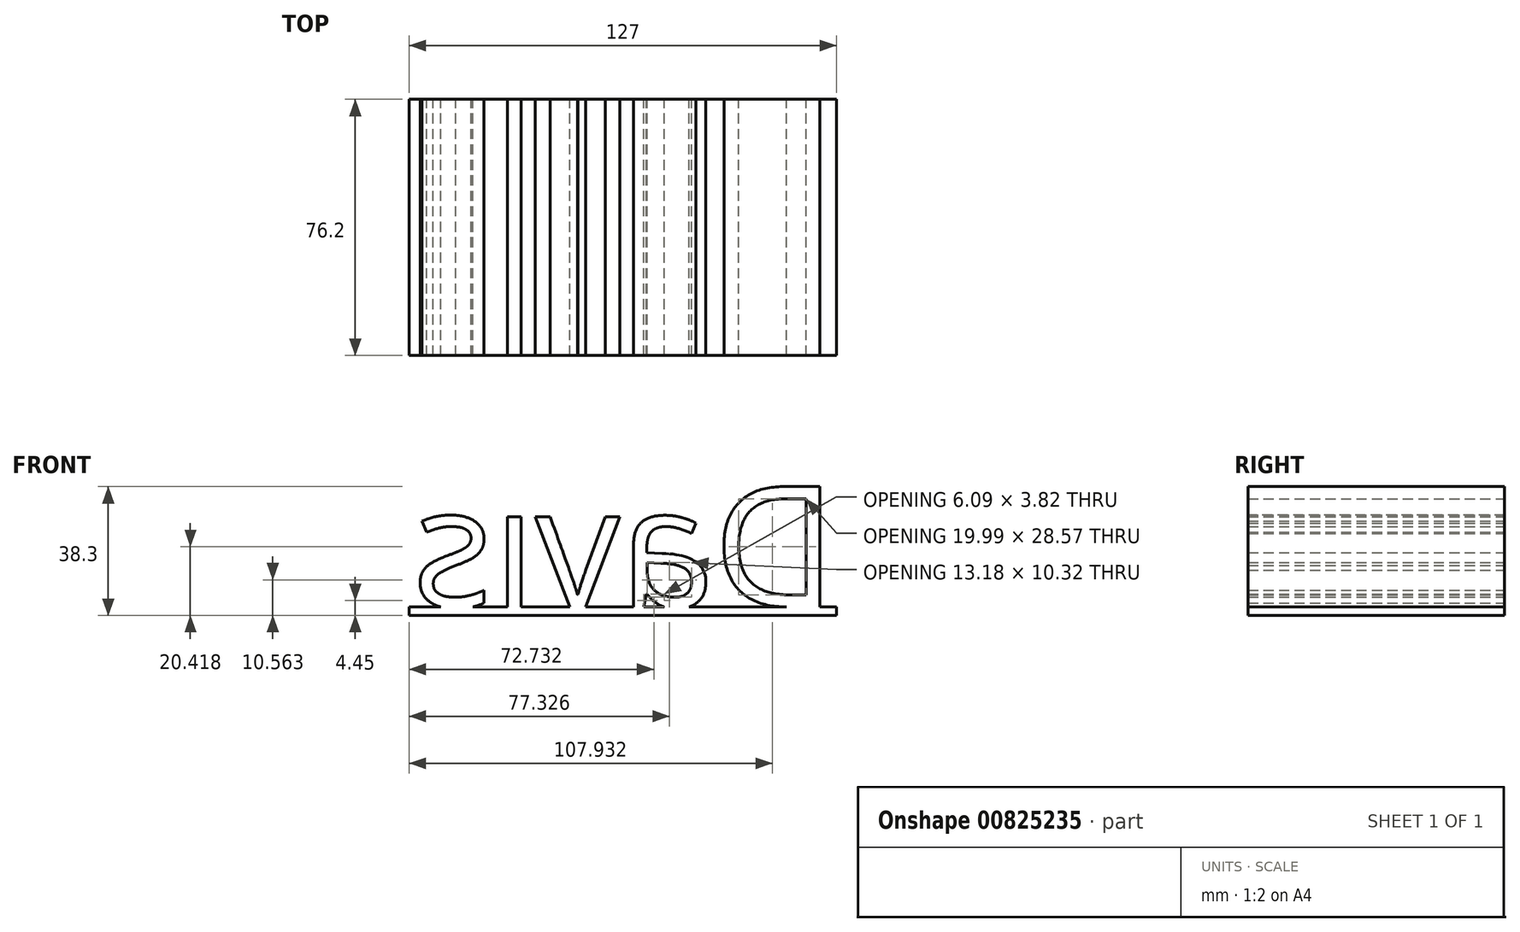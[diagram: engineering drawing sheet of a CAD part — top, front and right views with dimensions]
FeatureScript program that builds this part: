
annotation { "Feature Type Name" : "Feature", "Feature Type Description" : "" }
export const myFeature = defineFeature(function(context is Context, id is Id, definition is map)
    precondition{}
    {
        {
            var Q0;
            Q0=qCreatedBy(makeId("Front.planeOp"),FACE);
            var sketch = newSketch(context, id + "F0", { "sketchPlane" : qUnion([Q0])});
            skLineSegment(sketch, "E0.bottom", {"start": v(0, 0) * mm, "end": v(127, 0) * mm});
            skLineSegment(sketch, "E0.top", {"start": v(0, 2.54) * mm, "end": v(127, 2.54) * mm});
            skLineSegment(sketch, "E0.left", {"start": v(0, 0) * mm, "end": v(0, 2.54) * mm});
            skLineSegment(sketch, "E0.right", {"start": v(127, 0) * mm, "end": v(127, 2.54) * mm});
            skSolve(sketch);
        }
        {
            var Q0;
            Q0 = qSketchRegion(id + "F0", true);
            extrude(context, id + "F1", {"entities" : qUnion([Q0]), "depth" : 76.2 * mm, "offsetDistance" : 25.4 * mm});
        }
        {
            var Q0;
            Q0=makeQuery(id+"F1.opExtrude","CAP_FACE",FACE,{"disambiguationData":[OSD([sQuery(id+"F0.wireOp",EDGE,"E0.bottom"),sQuery(id+"F0.wireOp",EDGE,"E0.top"),sQuery(id+"F0.wireOp",EDGE,"E0.left"),sQuery(id+"F0.wireOp",EDGE,"E0.right")])],"isStart":true});
            var sketch = newSketch(context, id + "F2", { "sketchPlane" : qUnion([Q0])});
            skText(sketch, "E1", { "text": "Davis", "fontName": "OpenSans-Regular.ttf"});
            const initialGuessF2  = {"E1": [-0.127, 0.00254, 1, 0, 0.03607]};
            skSetInitialGuess(sketch, initialGuessF2);
            skSolve(sketch);
        }
        {
            var Q0;
            Q0 = qSketchRegion(id + "F2", true);
            extrude(context, id + "F3", {"entities" : qUnion([Q0]), "operationType" : NewBodyOperationType.ADD, "oppositeDirection" : true, "depth" : 76.2 * mm, "offsetDistance" : 25.4 * mm});
        }
        {
            var Q0;
            Q0=makeQuery(id+"F3.opExtrude","CAP_FACE",FACE,{"disambiguationData":[OSD([sQuery(id+"F2.wireOp",EDGE,"E1.sketch_text.stroke-55"),sQuery(id+"F2.wireOp",EDGE,"E1.sketch_text.stroke-56"),sQuery(id+"F2.wireOp",EDGE,"E1.sketch_text.stroke-57"),sQuery(id+"F2.wireOp",EDGE,"E1.sketch_text.stroke-58"),sQuery(id+"F2.wireOp",EDGE,"E1.sketch_text.stroke-59"),sQuery(id+"F2.wireOp",EDGE,"E1.sketch_text.stroke-60"),sQuery(id+"F2.wireOp",EDGE,"E1.sketch_text.stroke-61"),sQuery(id+"F2.wireOp",EDGE,"E1.sketch_text.stroke-62")])],"isStart":true});
            var sketch = newSketch(context, id + "F4", { "sketchPlane" : qUnion([Q0])});
            skLineSegment(sketch, "E2.bottom", {"start": v(-35.36, 43.85) * mm, "end": v(-27.44, 43.85) * mm});
            skLineSegment(sketch, "E2.top", {"start": v(-35.36, 33.3) * mm, "end": v(-27.44, 33.3) * mm});
            skLineSegment(sketch, "E2.left", {"start": v(-35.36, 43.85) * mm, "end": v(-35.36, 33.3) * mm});
            skLineSegment(sketch, "E2.right", {"start": v(-27.44, 43.85) * mm, "end": v(-27.44, 33.3) * mm});
            skSolve(sketch);
        }
        {
            var Q0;
            Q0 = qSketchRegion(id + "F4", true);
            extrude(context, id + "F5", {"entities" : qUnion([Q0]), "operationType" : NewBodyOperationType.REMOVE, "oppositeDirection" : true, "depth" : 127 * mm, "offsetDistance" : 25.4 * mm});
        }
    });
